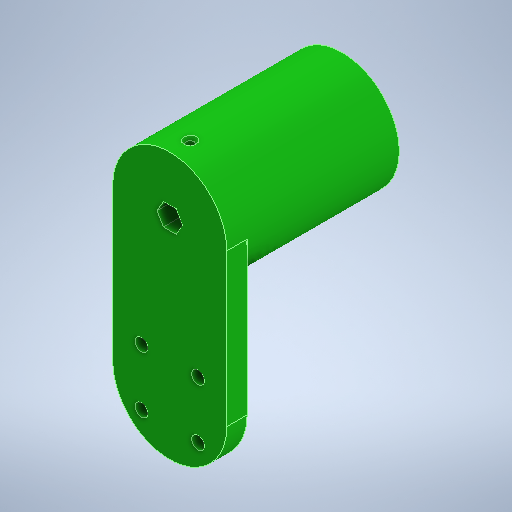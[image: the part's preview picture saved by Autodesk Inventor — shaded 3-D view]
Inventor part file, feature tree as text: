
AUTODESK INVENTOR PART (.ipt)
format: ipt  version: 2025.1 (Build 291241000, 241)  size: 297,984 bytes
history: native  units: mm
features: sketch x4, extrude x2, thicken_offset x1, plane x1, hole x1
ambient origin geometry x8: Origin, YZ Plane, XZ Plane, XY Plane, X Axis, Y Axis, Z Axis, Center Point
bodies: Solid1 (feature_tree)
feature tree (9):
  extrude  "Extrusion1"  Depth=5.0mm
  extrude  "Extrusion2"  Depth=11.14mm
  thicken_offset  "Thicken1"
  plane  "Work Plane1"
  hole  "Hole1"  [1 undecoded]
  sketch  "Sketch1"  dims[d0=45.0mm d3=5.0mm]
  sketch  "Sketch Circular Pattern1"  dims[d4=11.14mm d5=11.14mm]
  sketch  "Sketch2"  dims[d6=40.0mm d8=360.0deg d10=8.0mm d11=0.0mm]
  sketch  "Sketch4"  dims[d12=60.0mm d14=10.0mm d15=60.0mm d16=0.0mm d17=20.0mm d18=20.0mm d19=3.0mm d20=3.0mm d21=3.708mm d22=5.0mm d23=2.0mm d24=14.3117mm d25=18.5mm d26=0.0mm d27=60.0mm d28=60.0mm]
note: 1 required parameter value undecoded (feature->parameter linkage not recoverable at this tier; creation-order binding heuristic only, values carry confidence <= 0.55)
